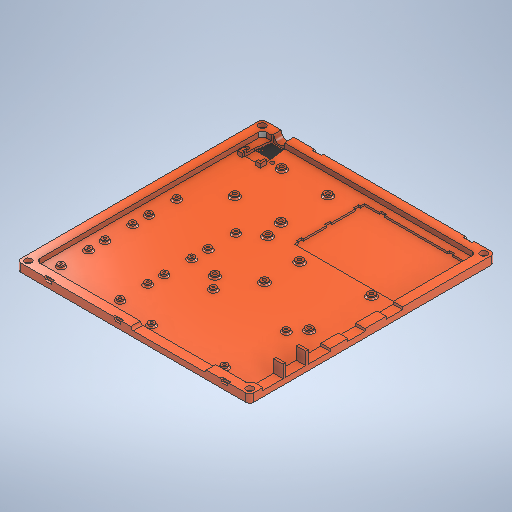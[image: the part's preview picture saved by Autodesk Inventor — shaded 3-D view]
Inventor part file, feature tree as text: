
AUTODESK INVENTOR PART (.ipt)
format: ipt  version: 2025.2 (Build 292293000, 293)  size: 991,744 bytes
history: native  units: mm
features: extrude x22, sketch x6, plane x6, fillet x4, chamfer x2, mirror x2, pattern_linear x1
ambient origin geometry x8: Origin, YZ Plane, XZ Plane, XY Plane, X Axis, Y Axis, Z Axis, Center Point
bodies: Solid1 (feature_tree)
feature tree (43):
  sketch  "Sketch1"  dims[d0=7.5mm d1=53.34mm]
  extrude  "Base"  Depth=53.34mm
  extrude  "Wall"  Depth=15.24mm
  extrude  "Breadboard slot"  Depth=2.54mm
  extrude  "Electronic mounting holes"  Depth=17.78mm
  extrude  "Extrusion33"  Depth=90.17mm
  chamfer  "Chamfer1"  Distance=45.72mm
  chamfer  "Chamfer2"  Distance=2.8mm
  extrude  "Deeper mounting holes"  Depth=5.8mm
  extrude  "Extrusion34"  Depth=5.8mm
  pattern_linear  "Rectangular Pattern3"  Spacing1=0.5mm  [1 undecoded]
  extrude  "Extrusion14"  Depth=5.8mm
  extrude  "Extrusion9"  Depth=1.5mm
  extrude  "Extrusion10"  Depth=10.0mm
  extrude  "Extrusion11"  Depth=5.8mm
  sketch  "Sketch4"  dims[d4=13.97mm d5=2.54mm]
  extrude  "Board Ports"  Depth=5.8mm
  fillet  "Fillet6"  Radius=2.0mm
  extrude  "Pi Opening Wall Raise"  Depth=5.8mm
  extrude  "DC jack opening"  Depth=5.8mm
  fillet  "Base corner fillets"  Radius=3.5mm
  plane  "Work Plane4"
  plane  "Work Plane5"
  plane  "Work Plane6"
  plane  "Work Plane7"
  sketch  "Sketch6"  dims[d9=66.04mm d10=90.17mm]
  extrude  "Snap fit point 1"  Depth=3.5mm
  extrude  "Snap fit point 2"  Depth=5.8mm
  extrude  "Snap fit point 3"  Depth=5.8mm
  extrude  "Snap fit point 4"  Depth=5.8mm
  extrude  "Snap fit point 5"  Depth=1.5mm
  fillet  "Fillet4"  Radius=2.0mm
  fillet  "Fillet5"  Radius=43.0mm
  sketch  "Sketch12"  dims[d11=96.52mm d12=45.72mm d13=2.8mm d15=54.75mm d16=81.68mm d17=0.5mm d18=4.0mm d19=1.5mm d20=30.0mm d22=22.7mm d23=10.0mm d25=10.0mm d27=11.9mm d28=54.53mm d29=2.0mm d31=56.0mm d32=85.0mm d33=3.5mm d34=3.5mm d35=1.8mm d37=52.5mm d38=61.5mm d39=1.5mm d40=2.0mm d44=43.0mm d47=30.0mm d48=17.0mm d50=2.871mm d51=3.32mm d52=2.8mm d55=1.5mm d56=40.244mm d57=40.057mm d59=10.5mm d63=14.0mm d65=1.6mm d66=0.8mm d67=1.2mm d68=0.8mm d69=1.2mm d70=0.8mm d71=1.2mm d72=0.8mm d73=1.2mm d74=0.8mm d75=1.2mm d76=0.8mm d77=9.5mm d78=-13.0mm d79=10.5mm d80=4.5mm d81=3.0mm d82=2.0mm d83=2.0mm d84=1.5mm d87=2.5mm d88=0.0mm d89=4.0mm d90=0.0mm d91=1.5mm d92=0.0mm d93=2.0mm d94=0.0mm d95=1.0mm d96=0.0mm d117=2.0mm d118=0.0mm d119=0.5mm d120=0.0mm d121=3.0mm d122=0.0mm d125=1.0mm d127=19.0mm d129=37.0mm d131=8.5mm d132=13.64mm d133=39.0mm d134=13.0mm d135=2.0mm d136=0.0mm d137=25.0mm d138=85.0mm d139=10.0mm d140=2.0mm d141=0.0mm d142=3.0mm d143=20.0mm d144=6.5mm d145=2.5mm d146=0.0mm d147=3.0mm d148=1.5mm d149=2.5mm d150=1.0mm d151=45.0deg d154=-20.0mm d155=-105.0mm d157=-140.0mm d158=5.0mm d159=0.0mm d160=5.0mm d161=0.0mm d162=-160.0mm d163=5.0mm d164=0.0mm d165=5.0mm d166=0.0mm d167=5.0mm d168=0.0mm d173=60.0mm d174=180.0mm d175=170.0mm d176=17.0mm d177=35.0mm d178=54.5mm d179=1.0mm d180=8.0mm d181=0.0mm d188=1.0mm d189=5.8mm d190=4.5mm d191=4.5mm d192=5.5mm d193=1.0mm d194=0.0mm d195=3.2mm d196=0.0mm d197=0.0mm d198=3.0mm d199=0.0mm d234=2.0mm d237=1.0mm d238=2.0mm d239=45.0deg d240=26.0mm d241=51.0mm d242=1.8mm d243=2.0mm d244=2.0mm d245=4.8mm d246=10.0mm d247=0.0mm d248=1.0mm d249=2.0mm d250=45.0deg d251=1.0mm d252=0.0mm d253=30.0mm d255=35.0mm d258=6.0mm d259=5.0mm d260=10.0mm d261=10.0mm d262=20.0mm d264=35.0mm d265=5.8mm d266=20.0mm]
  extrude  "Extrusion24"  Depth=5.8mm
  extrude  "Extrusion25"  Depth=5.8mm
  extrude  "Base mounting hole"  Depth=5.8mm
  plane  "Work Plane8"
  plane  "Work Plane9"
  mirror  "Mirror4"
  mirror  "Mirror5"
  sketch  "Sketch Rectangular Pattern1"  dims[d2=101.6mm d3=15.24mm]
  sketch  "Sketch5"  dims[d6=50.8mm d7=17.78mm]
note: 1 required parameter value undecoded (feature->parameter linkage not recoverable at this tier; creation-order binding heuristic only, values carry confidence <= 0.55)
